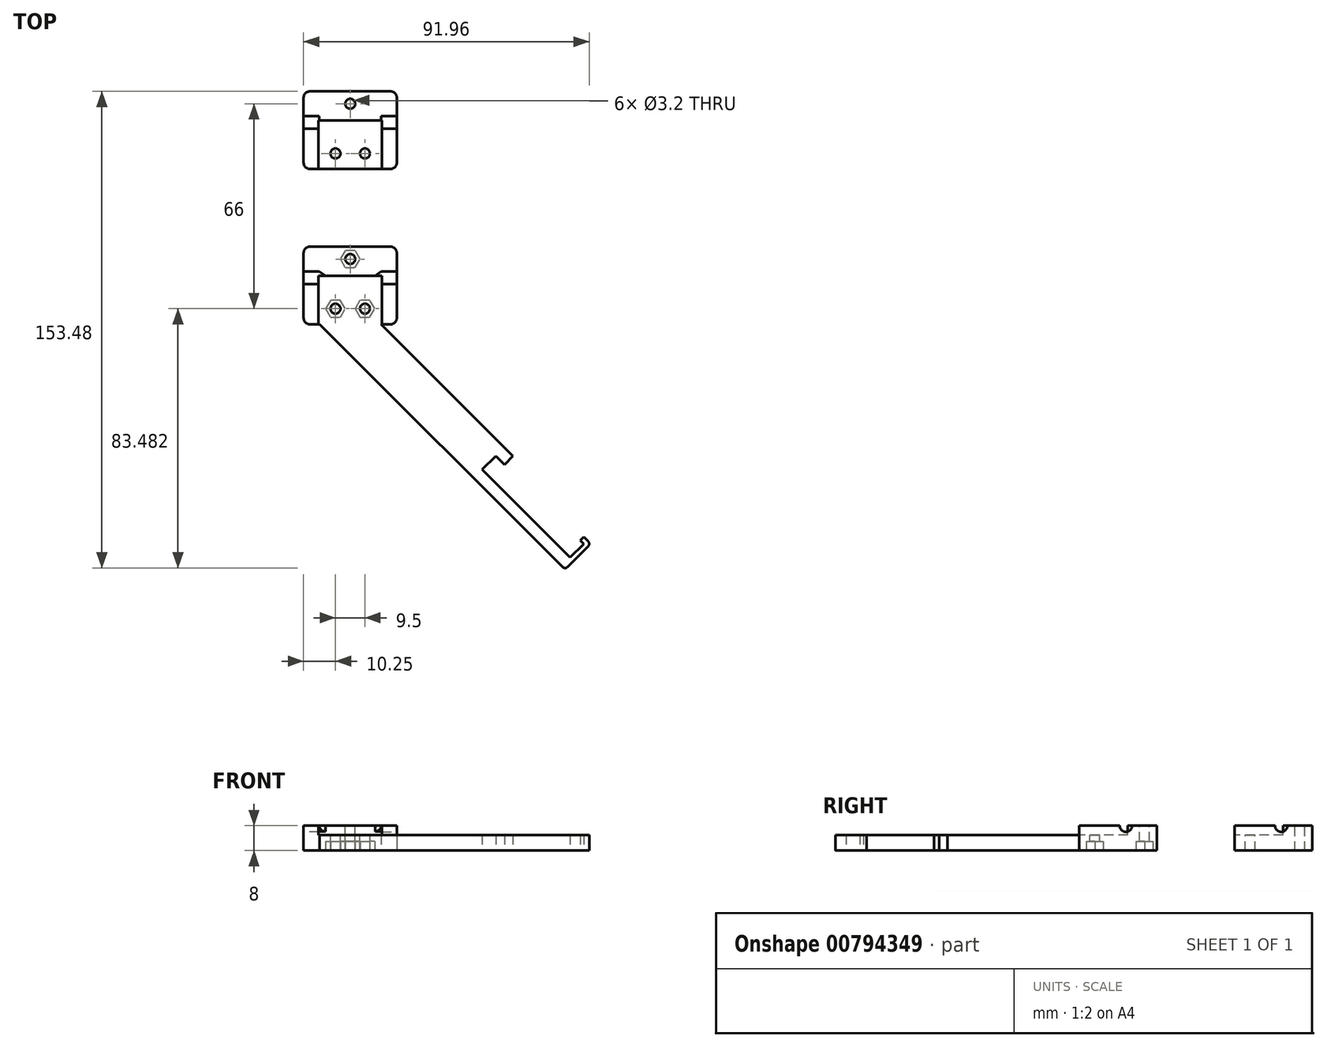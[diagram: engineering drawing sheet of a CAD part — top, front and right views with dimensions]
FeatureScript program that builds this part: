
annotation { "Feature Type Name" : "Feature", "Feature Type Description" : "" }
export const myFeature = defineFeature(function(context is Context, id is Id, definition is map)
    precondition{}
    {
        {
            var Q0;
            Q0=qCreatedBy(makeId("Top.planeOp"),FACE);
            var sketch = newSketch(context, id + "F0", { "sketchPlane" : qUnion([Q0])});
            skLineSegment(sketch, "E0.bottom", {"start": v(-13, 11.96) * mm, "end": v(13, 11.96) * mm});
            skLineSegment(sketch, "E0.top", {"start": v(-13, -13.04) * mm, "end": v(13, -13.04) * mm});
            skLineSegment(sketch, "E0.left", {"start": v(-15, 9.96) * mm, "end": v(-15, -11.04) * mm});
            skLineSegment(sketch, "E0.right", {"start": v(15, 9.96) * mm, "end": v(15, -11.04) * mm});
            skPoint(sketch, "E1.visualSharp", {"position": v(-15, 11.96) * mm});
            skArc(sketch, "E1.filletArc", {"start": v(-13, 11.96) * mm, "mid": v(-14.41, 11.38) * mm, "end": v(-15, 9.96) * mm});
            skPoint(sketch, "E2.visualSharp", {"position": v(15, 11.96) * mm});
            skArc(sketch, "E2.filletArc", {"start": v(15, 9.96) * mm, "mid": v(14.41, 11.38) * mm, "end": v(13, 11.96) * mm});
            skPoint(sketch, "E3.visualSharp", {"position": v(15, -13.04) * mm});
            skArc(sketch, "E3.filletArc", {"start": v(13, -13.04) * mm, "mid": v(14.41, -12.45) * mm, "end": v(15, -11.04) * mm});
            skPoint(sketch, "E4.visualSharp", {"position": v(-15, -13.04) * mm});
            skArc(sketch, "E4.filletArc", {"start": v(-15, -11.04) * mm, "mid": v(-14.41, -12.45) * mm, "end": v(-13, -13.04) * mm});
            skSolve(sketch);
        }
        {
            var Q0;
            Q0 = qSketchRegion(id + "F0", true);
            extrude(context, id + "F1", {"entities" : qUnion([Q0]), "depth" : 8 * mm, "offsetDistance" : 25 * mm});
        }
        {
            var Q0;
            Q0=makeQuery(id+"F1.opExtrude","CAP_FACE",FACE,{"disambiguationData":[OSD([sQuery(id+"F0.wireOp",EDGE,"E0.bottom"),sQuery(id+"F0.wireOp",EDGE,"E0.top"),sQuery(id+"F0.wireOp",EDGE,"E0.left"),sQuery(id+"F0.wireOp",EDGE,"E0.right"),sQuery(id+"F0.wireOp",EDGE,"E1.filletArc"),sQuery(id+"F0.wireOp",EDGE,"E2.filletArc"),sQuery(id+"F0.wireOp",EDGE,"E3.filletArc"),sQuery(id+"F0.wireOp",EDGE,"E4.filletArc")])],"isStart":false});
            var sketch = newSketch(context, id + "F2", { "sketchPlane" : qUnion([Q0])});
            skLineSegment(sketch, "E5.bottom", {"start": v(-10.2, 2.56) * mm, "end": v(10.2, 2.56) * mm});
            skLineSegment(sketch, "E5.top", {"start": v(-10.2, -13.04) * mm, "end": v(10.2, -13.04) * mm});
            skLineSegment(sketch, "E5.left", {"start": v(-10.2, 2.56) * mm, "end": v(-10.2, -13.04) * mm});
            skLineSegment(sketch, "E5.right", {"start": v(10.2, 2.56) * mm, "end": v(10.2, -13.04) * mm});
            skSolve(sketch);
        }
        {
            var Q0;
            Q0 = qSketchRegion(id + "F2", true);
            extrude(context, id + "F3", {"entities" : qUnion([Q0]), "operationType" : NewBodyOperationType.REMOVE, "oppositeDirection" : true, "depth" : 3 * mm, "offsetDistance" : 25 * mm});
        }
        {
            var Q0;
            Q0=makeQuery(id+"F1.opExtrude","SWEPT_FACE",FACE,{"disambiguationData":[OSD([sQuery(id+"F0.wireOp",EDGE,"E0.right")])]});
            var sketch = newSketch(context, id + "F4", { "sketchPlane" : qUnion([Q0])});
            skCircle(sketch, "E6", {"center": v(1.96, 8) * mm, "radius": 2 * mm});
            skSolve(sketch);
        }
        {
            var Q0;
            Q0 = qSketchRegion(id + "F4", true);
            extrude(context, id + "F5", {"entities" : qUnion([Q0]), "operationType" : NewBodyOperationType.REMOVE, "oppositeDirection" : true, "depth" : 5 * mm, "offsetDistance" : 25 * mm});
        }
        {
            var Q0;
            Q0=makeQuery(id+"F1.opExtrude","SWEPT_FACE",FACE,{"disambiguationData":[OSD([sQuery(id+"F0.wireOp",EDGE,"E0.left")])]});
            var sketch = newSketch(context, id + "F6", { "sketchPlane" : qUnion([Q0])});
            skCircle(sketch, "E7", {"center": v(-1.96, 8) * mm, "radius": 2 * mm});
            skSolve(sketch);
        }
        {
            var Q0;
            Q0 = qSketchRegion(id + "F6", true);
            extrude(context, id + "F7", {"entities" : qUnion([Q0]), "operationType" : NewBodyOperationType.REMOVE, "oppositeDirection" : true, "depth" : 5 * mm, "offsetDistance" : 25 * mm});
        }
        {
            var Q0;
            Q0=makeQuery(id+"F3.boolean.opBoolean","COPY",FACE,{"derivedFrom":makeQuery(id+"F3.opExtrude","CAP_FACE",FACE,{"disambiguationData":[OSD([sQuery(id+"F2.wireOp",EDGE,"E5.bottom"),sQuery(id+"F2.wireOp",EDGE,"E5.top"),sQuery(id+"F2.wireOp",EDGE,"E5.left"),sQuery(id+"F2.wireOp",EDGE,"E5.right")])],"isStart":false})});
            var sketch = newSketch(context, id + "F8", { "sketchPlane" : qUnion([Q0])});
            skCircle(sketch, "E8", {"center": v(-4.75, -8.04) * mm, "radius": 1.6 * mm});
            skCircle(sketch, "E9", {"center": v(4.75, -8.04) * mm, "radius": 1.6 * mm});
            skSolve(sketch);
        }
        {
            var Q0;
            Q0 = qSketchRegion(id + "F8", true);
            extrude(context, id + "F9", {"entities" : qUnion([Q0]), "operationType" : NewBodyOperationType.REMOVE, "endBound" : BoundingType.THROUGH_ALL, "oppositeDirection" : true, "depth" : 25 * mm, "offsetDistance" : 25 * mm});
        }
        {
            var Q0;
            {var subQ0=sQuery(id+"F0.wireOp",EDGE,"E1.filletArc");var subQ3=sQuery(id+"F0.wireOp",EDGE,"E0.left");var subQ7=sQuery(id+"F0.wireOp",EDGE,"E0.right");var subQ9=sQuery(id+"F0.wireOp",EDGE,"E0.bottom");var subQ10=makeQuery(id+"F1.opExtrude","SWEPT_FACE",FACE,{"disambiguationData":[OSD([subQ9])]});var subQ11=sQuery(id+"F0.wireOp",EDGE,"E2.filletArc");var subQ15=sQuery(id+"F0.wireOp",EDGE,"E0.top");var subQ16=sQuery(id+"F0.wireOp",EDGE,"E4.filletArc");Q0=makeQuery(id+"F7.boolean.opBoolean","SPLIT",FACE,{"disambiguationData":[TD([subQ10])],"derivedFrom":makeQuery(id+"F5.boolean.opBoolean","SPLIT",FACE,{"disambiguationData":[TD([subQ10])],"derivedFrom":makeQuery(id+"F1.opExtrude","CAP_FACE",FACE,{"disambiguationData":[OSD([subQ9,subQ15,subQ3,subQ7,subQ0,subQ11,sQuery(id+"F0.wireOp",EDGE,"E3.filletArc"),subQ16])],"isStart":false})})});}
            var sketch = newSketch(context, id + "F10", { "sketchPlane" : qUnion([Q0])});
            skCircle(sketch, "E10", {"center": v(0, 7.96) * mm, "radius": 1.6 * mm});
            skSolve(sketch);
        }
        {
            var Q0;
            Q0 = qSketchRegion(id + "F10", true);
            extrude(context, id + "F11", {"entities" : qUnion([Q0]), "operationType" : NewBodyOperationType.REMOVE, "endBound" : BoundingType.THROUGH_ALL, "oppositeDirection" : true, "depth" : 25 * mm, "offsetDistance" : 25 * mm});
        }
        {
            var Q0;
            Q0=makeQuery(id+"F1.opExtrude","SWEPT_BODY",BODY,{"disambiguationData":[OSD([sQuery(id+"F0.wireOp",EDGE,"E0.bottom"),sQuery(id+"F0.wireOp",EDGE,"E0.top"),sQuery(id+"F0.wireOp",EDGE,"E0.left"),sQuery(id+"F0.wireOp",EDGE,"E0.right"),sQuery(id+"F0.wireOp",EDGE,"E1.filletArc"),sQuery(id+"F0.wireOp",EDGE,"E2.filletArc"),sQuery(id+"F0.wireOp",EDGE,"E3.filletArc"),sQuery(id+"F0.wireOp",EDGE,"E4.filletArc")])]});
            var Q1;
            Q1=qCreatedBy(makeId("Front.planeOp"),FACE);
            transform(context, id + "F12", {"entities" : qUnion([Q0]), "transformType" : TransformType.TRANSLATION_DISTANCE, "transformDirection" : qUnion([Q1]), "distance" : 50 * mm, "makeCopy" : true});
        }
        {
            var Q0;
            Q0=makeQuery(id+"F12.opPattern","COPY",FACE,{"derivedFrom":makeQuery(id+"F1.opExtrude","CAP_FACE",FACE,{"disambiguationData":[OSD([sQuery(id+"F0.wireOp",EDGE,"E0.bottom"),sQuery(id+"F0.wireOp",EDGE,"E0.top"),sQuery(id+"F0.wireOp",EDGE,"E0.left"),sQuery(id+"F0.wireOp",EDGE,"E0.right"),sQuery(id+"F0.wireOp",EDGE,"E1.filletArc"),sQuery(id+"F0.wireOp",EDGE,"E2.filletArc"),sQuery(id+"F0.wireOp",EDGE,"E3.filletArc"),sQuery(id+"F0.wireOp",EDGE,"E4.filletArc")])],"isStart":true}),"instanceName":"1"});
            var sketch = newSketch(context, id + "F13", { "sketchPlane" : qUnion([Q0])});
            skCircle(sketch, "E11.cCircle", {"center": v(-4.75, 58.04) * mm, "radius": 2.75 * mm, "construction": true});
            skLineSegment(sketch, "E11.0", {"start": v(-1.57, 58.04) * mm, "end": v(-3.16, 55.29) * mm});
            skLineSegment(sketch, "E11.1", {"start": v(-3.16, 55.29) * mm, "end": v(-6.34, 55.29) * mm});
            skLineSegment(sketch, "E11.2", {"start": v(-6.34, 55.29) * mm, "end": v(-7.93, 58.04) * mm});
            skLineSegment(sketch, "E11.3", {"start": v(-7.93, 58.04) * mm, "end": v(-6.34, 60.79) * mm});
            skLineSegment(sketch, "E11.4", {"start": v(-6.34, 60.79) * mm, "end": v(-3.16, 60.79) * mm});
            skLineSegment(sketch, "E11.5", {"start": v(-3.16, 60.79) * mm, "end": v(-1.57, 58.04) * mm});
            skPoint(sketch, "E11.0.midPoint", {"position": v(-2.37, 56.66) * mm});
            skCircle(sketch, "E12.cCircle", {"center": v(4.75, 58.04) * mm, "radius": 2.75 * mm, "construction": true});
            skLineSegment(sketch, "E12.0", {"start": v(7.93, 58.04) * mm, "end": v(6.34, 55.29) * mm});
            skLineSegment(sketch, "E12.1", {"start": v(6.34, 55.29) * mm, "end": v(3.16, 55.29) * mm});
            skLineSegment(sketch, "E12.2", {"start": v(3.16, 55.29) * mm, "end": v(1.57, 58.04) * mm});
            skLineSegment(sketch, "E12.3", {"start": v(1.57, 58.04) * mm, "end": v(3.16, 60.79) * mm});
            skLineSegment(sketch, "E12.4", {"start": v(3.16, 60.79) * mm, "end": v(6.34, 60.79) * mm});
            skLineSegment(sketch, "E12.5", {"start": v(6.34, 60.79) * mm, "end": v(7.93, 58.04) * mm});
            skPoint(sketch, "E12.0.midPoint", {"position": v(7.13, 56.66) * mm});
            skCircle(sketch, "E13.cCircle", {"center": v(0, 42.04) * mm, "radius": 2.75 * mm, "construction": true});
            skLineSegment(sketch, "E13.0", {"start": v(1.59, 39.29) * mm, "end": v(-1.59, 39.29) * mm});
            skLineSegment(sketch, "E13.1", {"start": v(-1.59, 39.29) * mm, "end": v(-3.18, 42.04) * mm});
            skLineSegment(sketch, "E13.2", {"start": v(-3.18, 42.04) * mm, "end": v(-1.59, 44.79) * mm});
            skLineSegment(sketch, "E13.3", {"start": v(-1.59, 44.79) * mm, "end": v(1.59, 44.79) * mm});
            skLineSegment(sketch, "E13.4", {"start": v(1.59, 44.79) * mm, "end": v(3.18, 42.04) * mm});
            skLineSegment(sketch, "E13.5", {"start": v(3.18, 42.04) * mm, "end": v(1.59, 39.29) * mm});
            skPoint(sketch, "E13.0.midPoint", {"position": v(0, 39.29) * mm});
            skSolve(sketch);
        }
        {
            var Q0;
            Q0 = qSketchRegion(id + "F13", true);
            extrude(context, id + "F14", {"entities" : qUnion([Q0]), "operationType" : NewBodyOperationType.REMOVE, "oppositeDirection" : true, "depth" : 3 * mm, "offsetDistance" : 25 * mm});
        }
        {
            var Q0;
            Q0=makeQuery(id+"F13.imprint","IMPRINT",FACE,{"disambiguationData":[TD([[makeQuery(id+"F13.imprint","IMPRINT",EDGE,{"derivedFrom":sQuery(id+"F13.wireOp",EDGE,"E11.0")}),1.0]])]});
            var sketch = newSketch(context, id + "F15", { "sketchPlane" : qUnion([Q0])});
            skLineSegment(sketch, "E14", {"start": v(10, 63.04) * mm, "end": v(52.43, 105.46) * mm});
            skLineSegment(sketch, "E15", {"start": v(-9.8, 63.04) * mm, "end": v(68.34, 141.17) * mm});
            skLineSegment(sketch, "E16", {"start": v(52.43, 105.46) * mm, "end": v(49.67, 108.22) * mm});
            skLineSegment(sketch, "E17", {"start": v(49.67, 108.22) * mm, "end": v(46.91, 105.46) * mm});
            skLineSegment(sketch, "E18", {"start": v(46.91, 105.46) * mm, "end": v(42.53, 109.85) * mm});
            skLineSegment(sketch, "E19", {"start": v(42.53, 109.85) * mm, "end": v(70.81, 138.13) * mm});
            skLineSegment(sketch, "E20", {"start": v(70.81, 138.13) * mm, "end": v(75.2, 133.75) * mm});
            skLineSegment(sketch, "E21", {"start": v(75.2, 133.75) * mm, "end": v(74.06, 132.62) * mm});
            skLineSegment(sketch, "E22", {"start": v(74.06, 132.62) * mm, "end": v(75.2, 131.49) * mm});
            skLineSegment(sketch, "E23", {"start": v(75.2, 131.49) * mm, "end": v(76.6, 132.9) * mm});
            skLineSegment(sketch, "E24", {"start": v(76.6, 134.6) * mm, "end": v(70.03, 141.17) * mm});
            skPoint(sketch, "E25.visualSharp", {"position": v(77.46, 133.75) * mm});
            skArc(sketch, "E25.filletArc", {"start": v(76.6, 132.9) * mm, "mid": v(76.96, 133.75) * mm, "end": v(76.6, 134.6) * mm});
            skPoint(sketch, "E26.visualSharp", {"position": v(69.18, 142.02) * mm});
            skArc(sketch, "E26.filletArc", {"start": v(70.03, 141.17) * mm, "mid": v(69.18, 141.52) * mm, "end": v(68.34, 141.17) * mm});
            skLineSegment(sketch, "E27", {"start": v(-9.8, 63.04) * mm, "end": v(10, 63.04) * mm});
            skSolve(sketch);
        }
        {
            var Q0;
            Q0 = qSketchRegion(id + "F15", true);
            extrude(context, id + "F16", {"entities" : qUnion([Q0]), "operationType" : NewBodyOperationType.ADD, "oppositeDirection" : true, "depth" : 5 * mm, "offsetDistance" : 25 * mm});
        }
        {
            var Q0;
            Q0=makeQuery(id+"F12.opPattern","COPY",EDGE,{"derivedFrom":makeQuery(id+"F7.boolean.opBoolean","INTERSECT",EDGE,{"derivedFrom":[makeQuery(id+"F3.boolean.opBoolean","COPY",FACE,{"derivedFrom":makeQuery(id+"F3.opExtrude","SWEPT_FACE",FACE,{"disambiguationData":[OSD([sQuery(id+"F2.wireOp",EDGE,"E5.bottom")])]})}),makeQuery(id+"F7.opExtrude","CAP_FACE",FACE,{"disambiguationData":[OSD([sQuery(id+"F6.wireOp",EDGE,"E7")])],"isStart":false})]}),"instanceName":"1"});
            chamfer(context, id + "F17", {"entities" : qUnion([Q0]), "chamferType" : ChamferType.OFFSET_ANGLE, "width" : 2 * mm, "oppositeDirection" : false, "angle" : 35 * degree, "tangentPropagation" : true});
        }
        {
            var Q0;
            Q0=makeQuery(id+"F12.opPattern","COPY",EDGE,{"derivedFrom":makeQuery(id+"F5.boolean.opBoolean","INTERSECT",EDGE,{"derivedFrom":[makeQuery(id+"F3.boolean.opBoolean","COPY",FACE,{"derivedFrom":makeQuery(id+"F3.opExtrude","SWEPT_FACE",FACE,{"disambiguationData":[OSD([sQuery(id+"F2.wireOp",EDGE,"E5.bottom")])]})}),makeQuery(id+"F5.opExtrude","CAP_FACE",FACE,{"disambiguationData":[OSD([sQuery(id+"F4.wireOp",EDGE,"E6")])],"isStart":false})]}),"instanceName":"1"});
            chamfer(context, id + "F18", {"entities" : qUnion([Q0]), "chamferType" : ChamferType.OFFSET_ANGLE, "width" : 2 * mm, "oppositeDirection" : false, "angle" : 35 * degree, "tangentPropagation" : true});
        }
    });
